# Revit family: GR_Адаптер линейный_Муфта(n)_VL-F-КСД_R21
name_source: partatom
category: Соединительные детали воздуховодов
units: mm (PartAtom-declared; Revit-internal decimal feet)

## family parameters
Всегда вертикально = Да
Заголовок OmniClass = Metal Ducts
На основе рабочей плоскости = Нет
Номер OmniClass = 23.75.70.14.31
Общий = Нет
При загрузке вырезать с полостями = Нет
Размер круглого соединителя = Использовать диаметр
Тип детали = Мультипорт

## types (15) — shared parameters
ADSK_URL страницы изделия = https://grilles.ru
ADSK_Версия Revit = 2021
ADSK_Единица измерения = шт.
ADSK_Завод-изготовитель = ООО "ВЕНТРЕШЕТКИКОМ"
ADSK_Код изделия = 000191
ADSK_Количество = 1
ADSK_Материал = ADSK_Оцинкованная сталь
ADSK_Наименование = VL-F-КСД, адаптер вентиляционной решётки радиальный
Изготовитель = ООО "ВЕНТРЕШЕТКИКОМ"
Корпус_Металл_Толщина = 1 мм
Муфта_Металл_Толщина = 1 мм
zero-valued in all types: Отметка по умолчанию

## per-type parameters (varying)
| type | Корпус_Высота | Корпус_Длина | Решётка_Высота | Решётка_Положение_Центр |
| VL-F-КСД 1-20 | 182 мм | 94 мм | 54 мм | 47 мм |
| VL-F-КСД 1-30 | 182 мм | 104 мм | 64 мм | 52 мм |
| VL-F-КСД 1-40 | 222 мм | 114 мм | 74 мм | 57 мм |
| VL-F-КСД 1-50 | 222 мм | 124 мм | 84 мм | 62 мм |
| VL-F-КСД 1-60 | 272 мм | 134 мм | 94 мм | 67 мм |
| VL-F-КСД 1-70 | 272 мм | 144 мм | 104 мм | 72 мм |
| VL-F-КСД 2-20 | 222 мм | 134 мм | 94 мм | 67 мм |
| VL-F-КСД 2-25 | 222 мм | 144 мм | 104 мм | 72 мм |
| VL-F-КСД 2-30 | 222 мм | 154 мм | 114 мм | 77 мм |
| VL-F-КСД 3-20 | 222 мм | 174 мм | 134 мм | 87 мм |
| VL-F-КСД 3-25 | 222 мм | 189 мм | 149 мм | 95 мм |
| VL-F-КСД 3-30 | 222 мм | 204 мм | 164 мм | 102 мм |
| VL-F-КСД 4-20 | 272 мм | 214 мм | 174 мм | 107 мм |
| VL-F-КСД 4-25 | 272 мм | 234 мм | 194 мм | 117 мм |
| VL-F-КСД 4-30 | 272 мм | 254 мм | 214 мм | 127 мм |

note: column(s) folded — value = type name in every type: ADSK_Марка
